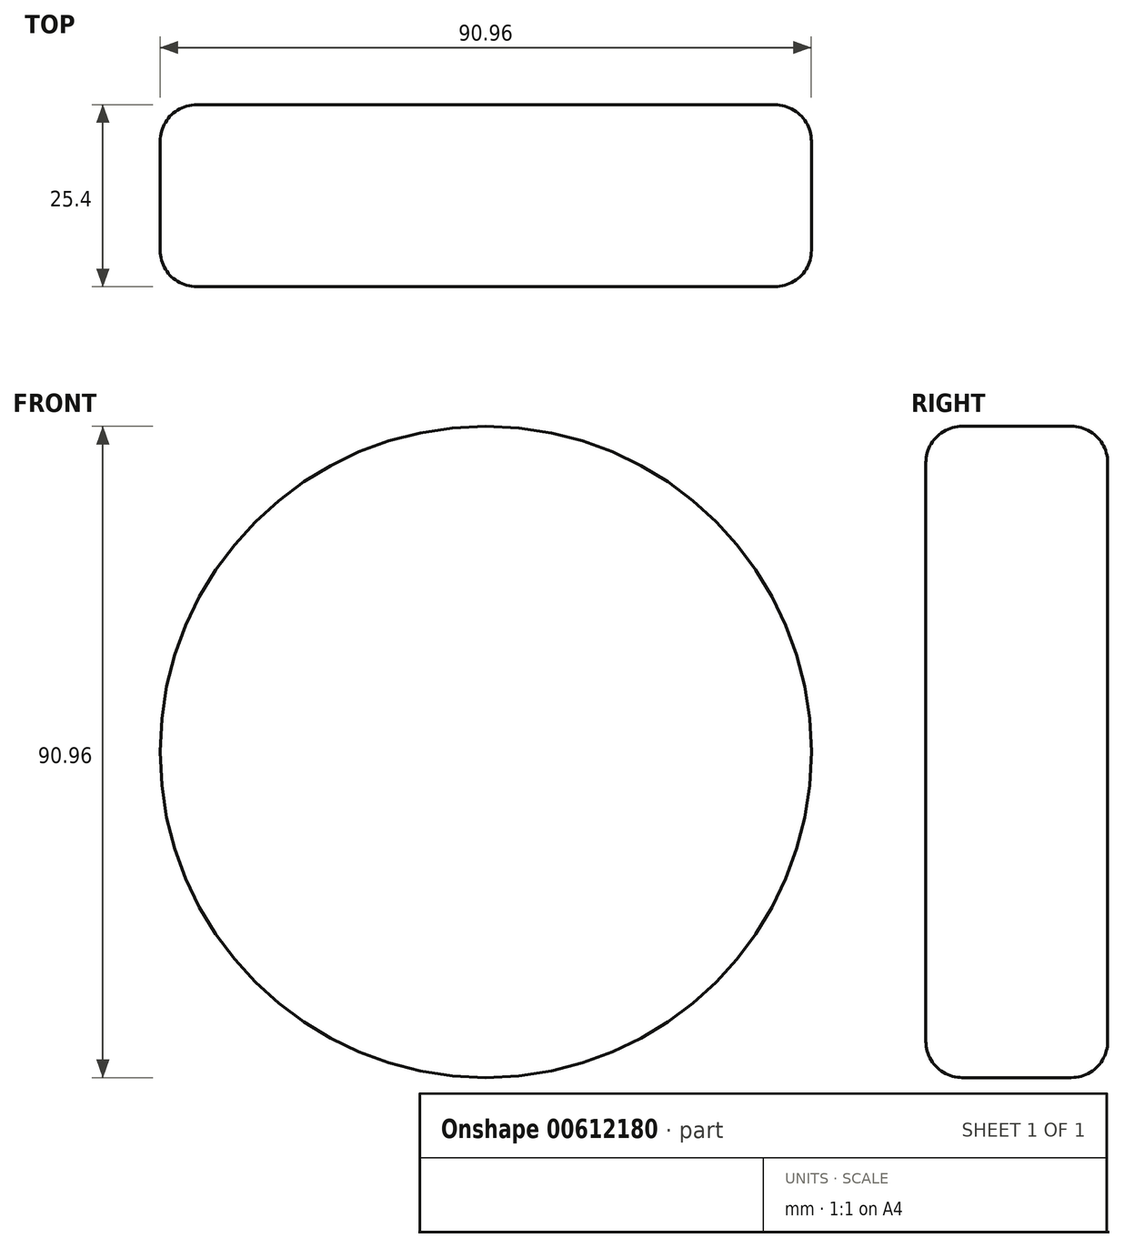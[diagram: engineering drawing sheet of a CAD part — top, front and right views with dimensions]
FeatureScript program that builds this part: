
annotation { "Feature Type Name" : "Feature", "Feature Type Description" : "" }
export const myFeature = defineFeature(function(context is Context, id is Id, definition is map)
    precondition{}
    {
        {
            var Q0;
            Q0=qCreatedBy(makeId("Front.planeOp"),FACE);
            var sketch = newSketch(context, id + "F0", { "sketchPlane" : qUnion([Q0])});
            skCircle(sketch, "E0", {"center": v(0, 0) * mm, "radius": 45.48 * mm});
            skSolve(sketch);
        }
        {
            var Q0;
            Q0=makeQuery(id+"F0.imprint","IMPRINT",FACE,{"disambiguationData":[TD([[makeQuery(id+"F0.imprint","IMPRINT",EDGE,{"derivedFrom":sQuery(id+"F0.wireOp",EDGE,"E0")}),1.0]])]});
            extrude(context, id + "F1", {"entities" : qUnion([Q0]), "depth" : 25.4 * mm, "offsetDistance" : 25.4 * mm});
        }
        {
            var Q0;
            Q0=makeQuery(id+"F1.opExtrude","SWEPT_FACE",FACE,{"disambiguationData":[OSD([sQuery(id+"F0.wireOp",EDGE,"E0")])]});
            fillet(context, id + "F2", {"entities" : qUnion([Q0]), "radius" : 5.08 * mm, "tangentPropagation" : true, "allowEdgeOverflow" : false});
        }
    });
